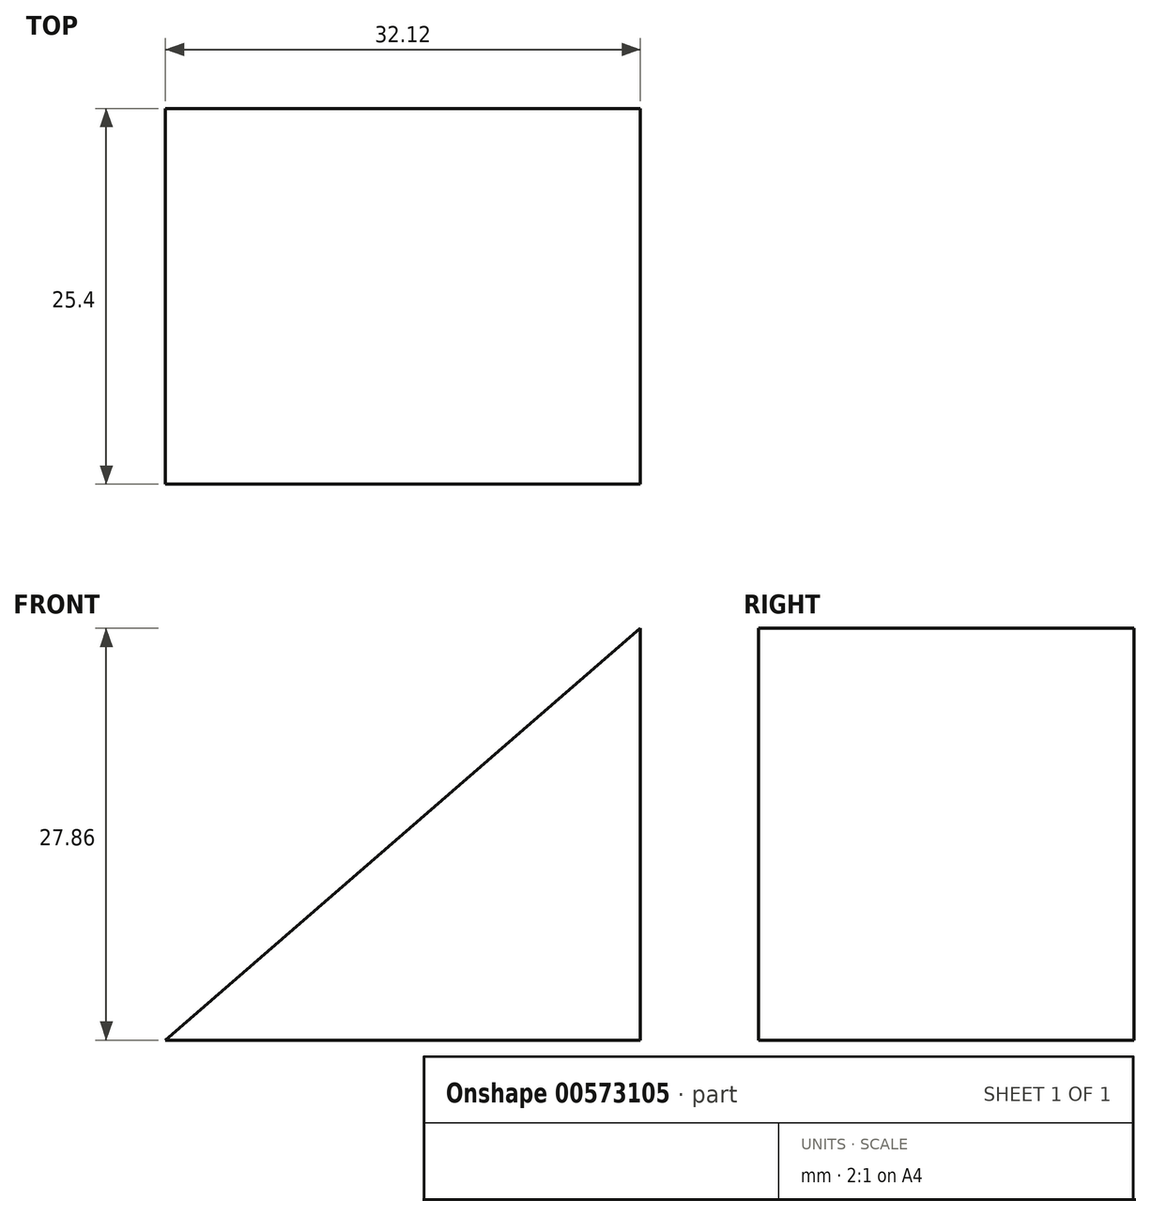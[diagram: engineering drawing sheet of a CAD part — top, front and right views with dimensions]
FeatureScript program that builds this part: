
annotation { "Feature Type Name" : "Feature", "Feature Type Description" : "" }
export const myFeature = defineFeature(function(context is Context, id is Id, definition is map)
    precondition{}
    {
        {
            var Q0;
            Q0=qCreatedBy(makeId("Front.planeOp"),FACE);
            var sketch = newSketch(context, id + "F0", { "sketchPlane" : qUnion([Q0])});
            skLineSegment(sketch, "E0", {"start": v(-32.12, 0) * mm, "end": v(0, 27.86) * mm});
            skLineSegment(sketch, "E1", {"start": v(0, 27.86) * mm, "end": v(0, 0) * mm});
            skLineSegment(sketch, "E2", {"start": v(-32.12, 0) * mm, "end": v(0, 0) * mm});
            skSolve(sketch);
        }
        {
            var Q0;
            Q0 = qSketchRegion(id + "F0", true);
            extrude(context, id + "F1", {"entities" : qUnion([Q0]), "depth" : 25.4 * mm, "offsetDistance" : 25.4 * mm});
        }
    });
